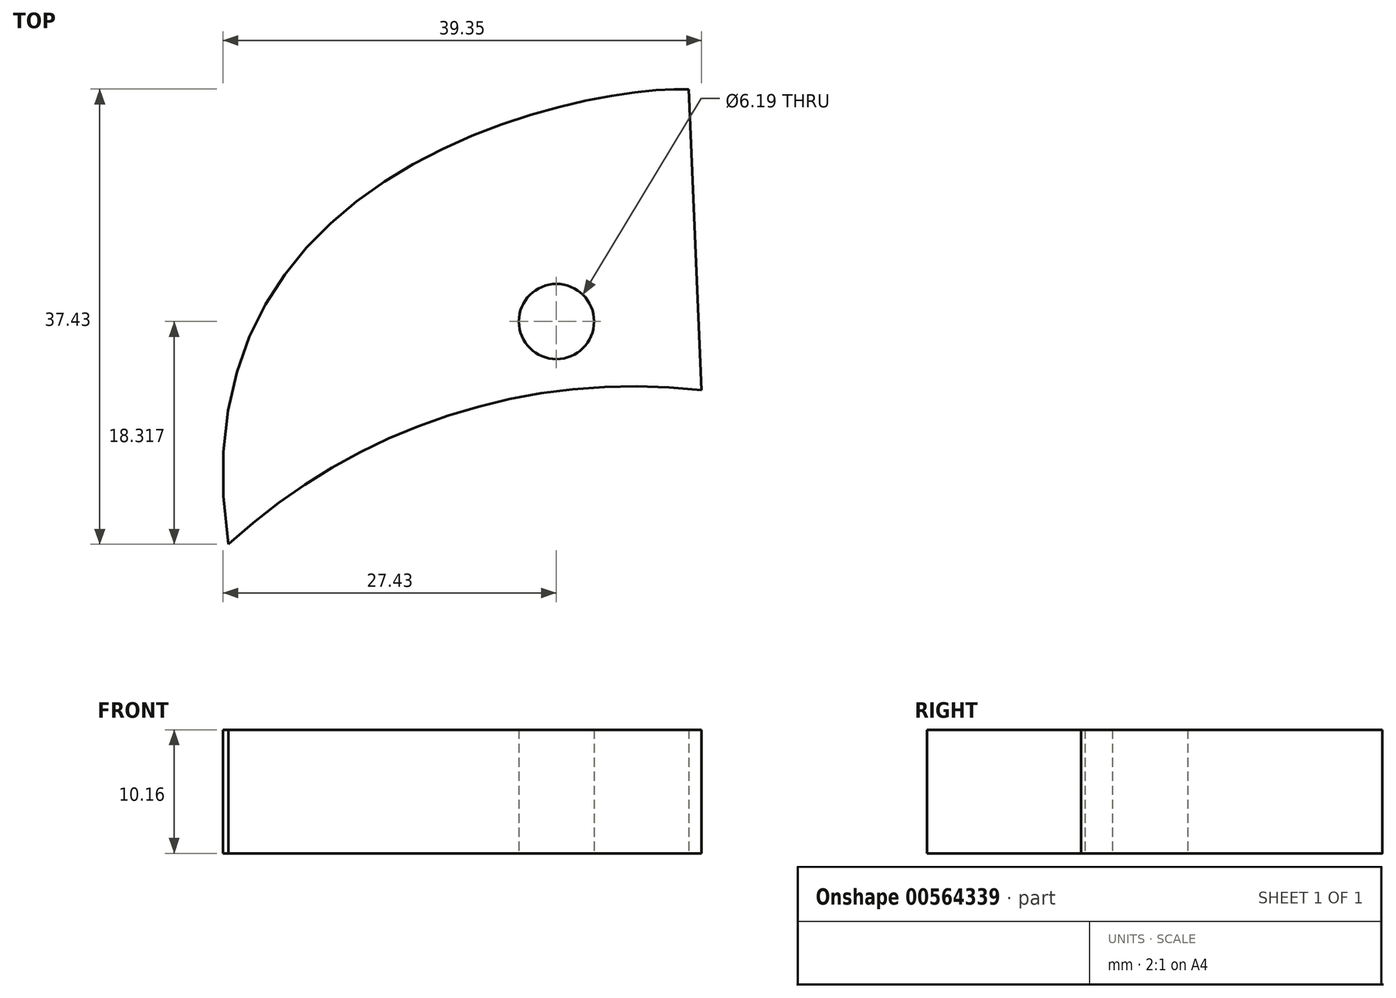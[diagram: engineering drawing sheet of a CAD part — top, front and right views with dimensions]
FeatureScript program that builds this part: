
annotation { "Feature Type Name" : "Feature", "Feature Type Description" : "" }
export const myFeature = defineFeature(function(context is Context, id is Id, definition is map)
    precondition{}
    {
        {
            var Q0;
            Q0=qCreatedBy(makeId("Top.planeOp"),FACE);
            var sketch = newSketch(context, id + "F0", { "sketchPlane" : qUnion([Q0])});
            skFitSpline(sketch, "E0", {"points": [v(10.88, 24.75) * mm, v(-26.96, -12.67) * mm], "startDerivative": vector(-24.9, 0.98) * mm, "endDerivative": vector(14.65, -93.78) * mm});
            skCircle(sketch, "E1", {"center": v(0, 5.65) * mm, "radius": 3.1 * mm});
            skLineSegment(sketch, "E2", {"start": v(10.88, 24.75) * mm, "end": v(11.92, 0) * mm});
            skArc(sketch, "E3", {"start": v(11.92, 0) * mm, "mid": v(-8.9, -2.09) * mm, "end": v(-26.96, -12.67) * mm});
            skSolve(sketch);
        }
        {
            var Q0;
            Q0=makeQuery(id+"F0.imprint","IMPRINT",FACE,{"disambiguationData":[TD([[makeQuery(id+"F0.imprint","IMPRINT",EDGE,{"derivedFrom":sQuery(id+"F0.wireOp",EDGE,"117dc65d-b370-497b-ae35-512844428b6d")}),-1.0]])]});
            var Q1;
            Q1=makeQuery(id+"F0.imprint","IMPRINT",FACE,{"disambiguationData":[TD([[makeQuery(id+"F0.imprint","IMPRINT",EDGE,{"derivedFrom":sQuery(id+"F0.wireOp",EDGE,"E0")}),1.0]])]});
            extrude(context, id + "F1", {"entities" : qUnion([Q0, Q1]), "depth" : 10.16 * mm, "offsetDistance" : 25.4 * mm});
        }
    });
